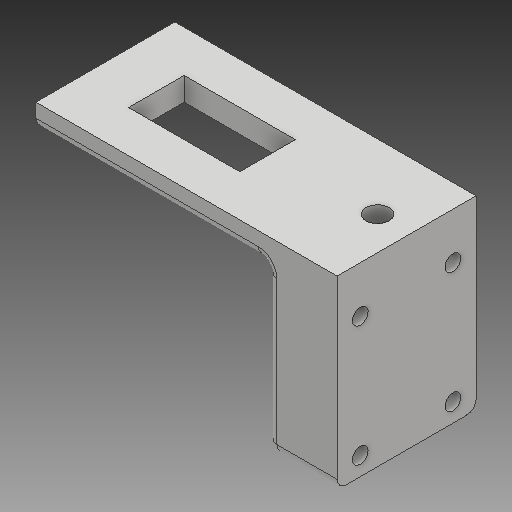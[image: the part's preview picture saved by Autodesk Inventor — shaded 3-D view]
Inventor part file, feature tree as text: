
AUTODESK INVENTOR PART (.ipt)
format: ipt  version: 2018 (Build 220112000, 112)  size: 136,704 bytes
history: native  units: mm
features: sketch x5, other x3
ambient origin geometry x8: Origin, YZ Plane, XZ Plane, XY Plane, X Axis, Y Axis, Z Axis, Center Point
bodies: Volumenkörper1 (feature_tree)
feature tree (8):
  other  "L-Halterung Servo_MIR1.ipt"
  other  "Volumenkörper1::L-Halterung Servo_MIR1.ipt"
  other  "Bezeichnung1"
  sketch  "Skizze1"  dims[d0=10.0mm]
  sketch  "Skizze2"
  sketch  "Skizze3"
  sketch  "Skizze4"
  sketch  "Skizze5"
